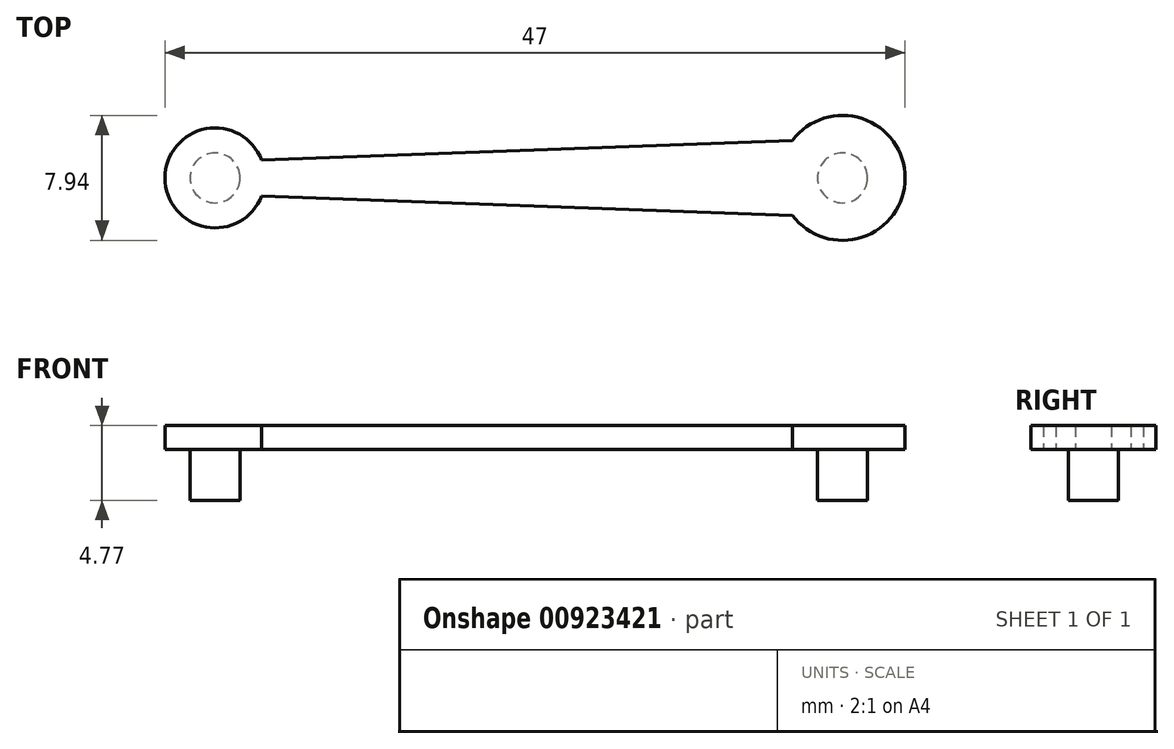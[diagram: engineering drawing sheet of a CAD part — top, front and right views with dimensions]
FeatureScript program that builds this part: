
annotation { "Feature Type Name" : "Feature", "Feature Type Description" : "" }
export const myFeature = defineFeature(function(context is Context, id is Id, definition is map)
    precondition{}
    {
        {
            var Q0;
            Q0=qCreatedBy(makeId("Top.planeOp"),FACE);
            var sketch = newSketch(context, id + "F0", { "sketchPlane" : qUnion([Q0])});
            skCircle(sketch, "E0", {"center": v(0, 0) * mm, "radius": 1.59 * mm});
            skCircle(sketch, "E1", {"center": v(-39.85, 0) * mm, "radius": 1.59 * mm});
            skArc(sketch, "E2", {"start": v(-3.18, -2.38) * mm, "mid": v(3.97, 0) * mm, "end": v(-3.17, 2.38) * mm});
            skArc(sketch, "E3", {"start": v(-36.9, 1.14) * mm, "mid": v(-43.03, 0) * mm, "end": v(-36.9, -1.14) * mm});
            skLineSegment(sketch, "E4", {"start": v(-36.9, 1.14) * mm, "end": v(-3.17, 2.38) * mm});
            skLineSegment(sketch, "E5", {"start": v(-3.17, -2.38) * mm, "end": v(-36.9, -1.14) * mm});
            skSolve(sketch);
        }
        {
            var Q0;
            Q0=qSketchRegion(id+"F0",true);
            extrude(context, id + "F1", {"entities" : qUnion([Q0]), "depth" : 1.52 * mm, "offsetDistance" : 25.4 * mm});
        }
        {
            var Q0;
            Q0=makeQuery(id+"F1.opExtrude","CAP_FACE",FACE,{"disambiguationData":[OSD([sQuery(id+"F0.wireOp",EDGE,"E0"),sQuery(id+"F0.wireOp",EDGE,"E1"),sQuery(id+"F0.wireOp",EDGE,"E2"),sQuery(id+"F0.wireOp",EDGE,"E3"),sQuery(id+"F0.wireOp",EDGE,"E4"),sQuery(id+"F0.wireOp",EDGE,"E5")])],"isStart":false});
            var sketch = newSketch(context, id + "F2", { "sketchPlane" : qUnion([Q0])});
            skCircle(sketch, "E6", {"center": v(-39.85, 0) * mm, "radius": 1.59 * mm});
            skCircle(sketch, "E7", {"center": v(0, 0) * mm, "radius": 1.59 * mm});
            skSolve(sketch);
        }
        {
            var Q0;
            Q0 = qSketchRegion(id + "F2", true);
            extrude(context, id + "F3", {"entities" : qUnion([Q0]), "operationType" : NewBodyOperationType.ADD, "oppositeDirection" : true, "depth" : 4.78 * mm, "offsetDistance" : 25.4 * mm});
        }
    });
